# Revit family: eckverbinder
name_source: partatom
category: Generic Models
revit_build: Autodesk Revit 2017 (Build: 20160225_1515(x64)
units: mm (PartAtom-declared; Revit-internal decimal feet)

## family parameters
Always vertical = Yes
Can host rebar = No
Cut with Voids When Loaded = No
Part Type = Normal
Room Calculation Point = No
Round Connector Dimension = Use Diameter
Shared = No
Work Plane-Based = No

## types (4) — shared parameters
Manufacturer = OBO BETTERMANN
URL = http://www.obo-bettermann.com

## per-type parameters (varying)
| type | Article Type | GTIN | Manufacturer Art.No. | Material |
| GEV 36 FT | GEV 36 FT | 4012196013272 | 6016723 | Hot-dip galvanised |
| GEV 36 G | GEV 36 FT | 4012196307876 | 6016715 | Electro-galvanised |
| GEV 36 A2 | GEV 36 A2 | 4012196013333 | 6016731 | Stainless steel, A2 |
| GEV 36 A4 | GEV 36 A4 | 4012196120253 | 6016764 | Stainless steel, A4 |

## geometry (parser evidence)
native form markers: Sweep x2
no freeform markers — native parametric forms only
